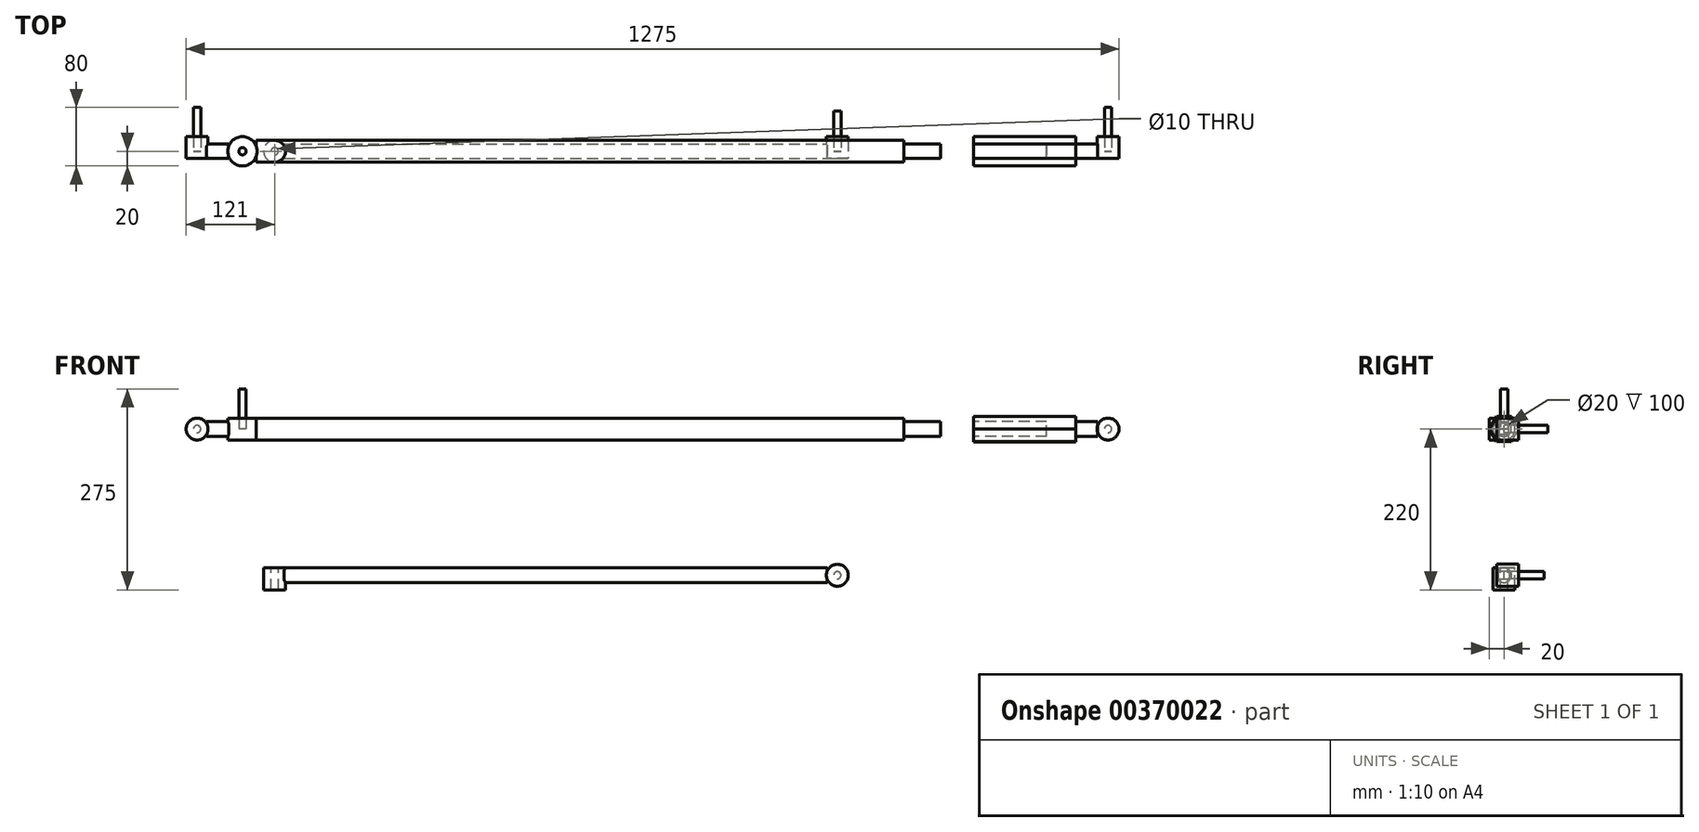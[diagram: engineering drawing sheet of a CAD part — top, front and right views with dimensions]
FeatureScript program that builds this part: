
annotation { "Feature Type Name" : "Feature", "Feature Type Description" : "" }
export const myFeature = defineFeature(function(context is Context, id is Id, definition is map)
    precondition{}
    {
        {
            var Q0;
            Q0=qCreatedBy(makeId("Right.planeOp"),FACE);
            var sketch = newSketch(context, id + "F0", { "sketchPlane" : qUnion([Q0])});
            skCircle(sketch, "E0", {"center": v(0, 0) * mm, "radius": 20 * mm});
            skCircle(sketch, "E1.cCircle", {"center": v(0, 0) * mm, "radius": 20 * mm, "construction": true});
            skLineSegment(sketch, "E1.0", {"start": v(10.09, 17.27) * mm, "end": v(20, -0.1) * mm});
            skLineSegment(sketch, "E1.1", {"start": v(20, -0.1) * mm, "end": v(9.91, -17.37) * mm});
            skLineSegment(sketch, "E1.2", {"start": v(9.91, -17.37) * mm, "end": v(-10.09, -17.27) * mm});
            skLineSegment(sketch, "E1.3", {"start": v(-10.09, -17.27) * mm, "end": v(-20, 0.1) * mm});
            skLineSegment(sketch, "E1.4", {"start": v(-20, 0.1) * mm, "end": v(-9.91, 17.37) * mm});
            skLineSegment(sketch, "E1.5", {"start": v(-9.91, 17.37) * mm, "end": v(10.09, 17.27) * mm});
            skCircle(sketch, "E2", {"center": v(0, 0) * mm, "radius": 10 * mm});
            skSolve(sketch);
        }
        {
            var Q0;
            Q0=makeQuery(id+"F0.imprint","IMPRINT",FACE,{"disambiguationData":[TD([[makeQuery(id+"F0.imprint","IMPRINT",EDGE,{"derivedFrom":sQuery(id+"F0.wireOp",EDGE,"E1.0")}),-1.0]])]});
            extrude(context, id + "F1", {"entities" : qUnion([Q0]), "depth" : 140 * mm});
        }
        {
            var Q0;
            Q0=qCreatedBy(makeId("Right.planeOp"),FACE);
            cPlane(context, id + "F2", {"entities" : qUnion([Q0]), "cplaneType" : CPlaneType.OFFSET, "offset" : 100 * mm, "width" : 150 * mm, "height" : 150 * mm});
        }
        {
            var Q0;
            Q0=qCreatedBy(id+"F2.planeOp",FACE);
            var sketch = newSketch(context, id + "F3", { "sketchPlane" : qUnion([Q0])});
            skCircle(sketch, "E3.0", {"center": v(0, 0) * mm, "radius": 10 * mm});
            skSolve(sketch);
        }
        {
            var Q0;
            Q0=qSketchRegion(id+"F3",true);
            extrude(context, id + "F4", {"entities" : qUnion([Q0]), "operationType" : NewBodyOperationType.ADD, "depth" : 70 * mm});
        }
        {
            var Q0;
            Q0=qCreatedBy(makeId("Front.planeOp"),FACE);
            cPlane(context, id + "F5", {"entities" : qUnion([Q0]), "cplaneType" : CPlaneType.OFFSET, "offset" : 10 * mm, "width" : 150 * mm, "height" : 150 * mm});
        }
        {
            var Q0;
            Q0=qCreatedBy(id+"F5.planeOp",FACE);
            var sketch = newSketch(context, id + "F6", { "sketchPlane" : qUnion([Q0])});
            skLineSegment(sketch, "E4", {"start": v(0, 0) * mm, "end": v(184, 0) * mm});
            skCircle(sketch, "E5", {"center": v(184, 0) * mm, "radius": 15 * mm});
            skSolve(sketch);
        }
        {
            var Q0;
            Q0=qSketchRegion(id+"F6",true);
            extrude(context, id + "F7", {"entities" : qUnion([Q0]), "oppositeDirection" : true, "depth" : 30 * mm});
        }
        {
            var Q0;
            Q0=qCreatedBy(makeId("Front.planeOp"),FACE);
            var sketch = newSketch(context, id + "F8", { "sketchPlane" : qUnion([Q0])});
            skLineSegment(sketch, "E6", {"start": v(0, 0) * mm, "end": v(184, 0) * mm});
            skCircle(sketch, "E7", {"center": v(184, 0) * mm, "radius": 5 * mm});
            skSolve(sketch);
        }
        {
            var Q0;
            Q0=qSketchRegion(id+"F8",true);
            extrude(context, id + "F9", {"entities" : qUnion([Q0]), "oppositeDirection" : true, "depth" : 60 * mm});
        }
        {
            var Q0;
            Q0=qCreatedBy(makeId("Front.planeOp"),FACE);
            var sketch = newSketch(context, id + "F10", { "sketchPlane" : qUnion([Q0])});
            skLineSegment(sketch, "E8", {"start": v(-45, 0) * mm, "end": v(-980, 0) * mm});
            skLineSegment(sketch, "E9", {"start": v(-45, 0) * mm, "end": v(-45, 10) * mm});
            skLineSegment(sketch, "E10", {"start": v(-45, 10) * mm, "end": v(-95, 10) * mm});
            skLineSegment(sketch, "E11", {"start": v(-95, 10) * mm, "end": v(-95, 15) * mm});
            skLineSegment(sketch, "E12", {"start": v(-95, 15) * mm, "end": v(-980, 15) * mm});
            skLineSegment(sketch, "E13", {"start": v(-980, 15) * mm, "end": v(-980, 0) * mm});
            skSolve(sketch);
        }
        {
            var Q0;
            Q0=makeQuery(id+"F10.imprint","IMPRINT",FACE,{"disambiguationData":[TD([[makeQuery(id+"F10.imprint","IMPRINT",EDGE,{"derivedFrom":sQuery(id+"F10.wireOp",EDGE,"E8")}),-1.0]])]});
            var Q1;
            Q1=sQuery(id+"F10.wireOp",EDGE,"E8");
            revolve(context, id + "F11", {"entities" : qUnion([Q0]), "axis" : qUnion([Q1]), "revolveType" : RevolveType.FULL});
        }
        {
            var Q0;
            Q0=qCreatedBy(makeId("Top.planeOp"),FACE);
            cPlane(context, id + "F12", {"entities" : qUnion([Q0]), "cplaneType" : CPlaneType.OFFSET, "offset" : 15 * mm, "width" : 150 * mm, "height" : 150 * mm});
        }
        {
            var Q0;
            Q0=qCreatedBy(id+"F12.planeOp",FACE);
            var sketch = newSketch(context, id + "F13", { "sketchPlane" : qUnion([Q0])});
            skLineSegment(sketch, "E14", {"start": v(0, 0) * mm, "end": v(-999, 0) * mm});
            skCircle(sketch, "E15", {"center": v(-999, 0) * mm, "radius": 20 * mm});
            skSolve(sketch);
        }
        {
            var Q0;
            Q0=qSketchRegion(id+"F13",true);
            extrude(context, id + "F14", {"entities" : qUnion([Q0]), "operationType" : NewBodyOperationType.ADD, "oppositeDirection" : true, "depth" : 30 * mm});
        }
        {
            var Q0;
            Q0=qCreatedBy(makeId("Top.planeOp"),FACE);
            var sketch = newSketch(context, id + "F15", { "sketchPlane" : qUnion([Q0])});
            skLineSegment(sketch, "E16", {"start": v(0, 0) * mm, "end": v(-999, 0) * mm});
            skCircle(sketch, "E17", {"center": v(-999, 0) * mm, "radius": 5 * mm});
            skSolve(sketch);
        }
        {
            var Q0;
            Q0=qSketchRegion(id+"F15",true);
            extrude(context, id + "F16", {"entities" : qUnion([Q0]), "depth" : 55 * mm});
        }
        {
            var Q0;
            Q0=qCreatedBy(makeId("Top.planeOp"),FACE);
            var sketch = newSketch(context, id + "F17", { "sketchPlane" : qUnion([Q0])});
            skLineSegment(sketch, "E18", {"start": v(0, 0) * mm, "end": v(-1018, 0) * mm});
            skLineSegment(sketch, "E19", {"start": v(-1018, 0) * mm, "end": v(-1048, 0) * mm});
            skLineSegment(sketch, "E20", {"start": v(-1048, 0) * mm, "end": v(-1048, 10) * mm});
            skLineSegment(sketch, "E21", {"start": v(-1048, 10) * mm, "end": v(-1018, 10) * mm});
            skLineSegment(sketch, "E22", {"start": v(-1018, 10) * mm, "end": v(-1018, 0) * mm});
            skSolve(sketch);
        }
        {
            var Q0;
            Q0=qSketchRegion(id+"F17",true);
            var Q1;
            Q1=sQuery(id+"F17.wireOp",EDGE,"E19");
            revolve(context, id + "F18", {"operationType" : NewBodyOperationType.ADD, "entities" : qUnion([Q0]), "axis" : qUnion([Q1]), "revolveType" : RevolveType.FULL});
        }
        {
            var Q0;
            Q0=qCreatedBy(id+"F5.planeOp",FACE);
            var sketch = newSketch(context, id + "F19", { "sketchPlane" : qUnion([Q0])});
            skLineSegment(sketch, "E23", {"start": v(0, 0) * mm, "end": v(-1061, 0) * mm});
            skCircle(sketch, "E24", {"center": v(-1061, 0) * mm, "radius": 15 * mm});
            skSolve(sketch);
        }
        {
            var Q0;
            Q0=qSketchRegion(id+"F19",true);
            extrude(context, id + "F20", {"entities" : qUnion([Q0]), "operationType" : NewBodyOperationType.ADD, "oppositeDirection" : true, "depth" : 30 * mm});
        }
        {
            var Q0;
            Q0=qCreatedBy(makeId("Front.planeOp"),FACE);
            var sketch = newSketch(context, id + "F21", { "sketchPlane" : qUnion([Q0])});
            skLineSegment(sketch, "E25", {"start": v(0, 0) * mm, "end": v(-1061, 0) * mm});
            skCircle(sketch, "E26", {"center": v(-1061, 0) * mm, "radius": 5 * mm});
            skSolve(sketch);
        }
        {
            var Q0;
            Q0=qSketchRegion(id+"F21",true);
            extrude(context, id + "F22", {"entities" : qUnion([Q0]), "oppositeDirection" : true, "depth" : 60 * mm});
        }
        {
            var Q0;
            Q0=qCreatedBy(makeId("Front.planeOp"),FACE);
            var sketch = newSketch(context, id + "F23", { "sketchPlane" : qUnion([Q0])});
            skLineSegment(sketch, "E27", {"start": v(0, 0) * mm, "end": v(0, -200) * mm});
            skLineSegment(sketch, "E28", {"start": v(0, -200) * mm, "end": v(-200, -200) * mm});
            skLineSegment(sketch, "E29", {"start": v(-200, -200) * mm, "end": v(-942, -200) * mm});
            skLineSegment(sketch, "E30", {"start": v(-942, -200) * mm, "end": v(-942, -190) * mm});
            skLineSegment(sketch, "E31", {"start": v(-942, -190) * mm, "end": v(-200, -190) * mm});
            skLineSegment(sketch, "E32", {"start": v(-200, -190) * mm, "end": v(-200, -200) * mm});
            skSolve(sketch);
        }
        {
            var Q0;
            Q0=qSketchRegion(id+"F23",true);
            var Q1;
            Q1=sQuery(id+"F23.wireOp",EDGE,"E29");
            revolve(context, id + "F24", {"entities" : qUnion([Q0]), "axis" : qUnion([Q1]), "revolveType" : RevolveType.FULL});
        }
        {
            var Q0;
            Q0=qCreatedBy(id+"F5.planeOp",FACE);
            var sketch = newSketch(context, id + "F25", { "sketchPlane" : qUnion([Q0])});
            skLineSegment(sketch, "E33", {"start": v(0, 0) * mm, "end": v(0, -200) * mm});
            skLineSegment(sketch, "E34", {"start": v(0, -200) * mm, "end": v(-186, -200) * mm});
            skCircle(sketch, "E35", {"center": v(-186, -200) * mm, "radius": 15 * mm});
            skSolve(sketch);
        }
        {
            var Q0;
            Q0=qSketchRegion(id+"F25",true);
            extrude(context, id + "F26", {"entities" : qUnion([Q0]), "operationType" : NewBodyOperationType.ADD, "oppositeDirection" : true, "depth" : 30 * mm});
        }
        {
            var Q0;
            Q0=qCreatedBy(makeId("Front.planeOp"),FACE);
            var sketch = newSketch(context, id + "F27", { "sketchPlane" : qUnion([Q0])});
            skLineSegment(sketch, "E36", {"start": v(0, 0) * mm, "end": v(0, -200) * mm});
            skLineSegment(sketch, "E37", {"start": v(0, -200) * mm, "end": v(-186, -200) * mm});
            skCircle(sketch, "E38", {"center": v(-186, -200) * mm, "radius": 5 * mm});
            skSolve(sketch);
        }
        {
            var Q0;
            Q0=qSketchRegion(id+"F27",true);
            extrude(context, id + "F28", {"entities" : qUnion([Q0]), "oppositeDirection" : true, "depth" : 55 * mm});
        }
        {
            var Q0;
            Q0=qCreatedBy(makeId("Top.planeOp"),FACE);
            cPlane(context, id + "F29", {"entities" : qUnion([Q0]), "cplaneType" : CPlaneType.OFFSET, "offset" : 190 * mm, "oppositeDirection" : true, "width" : 150 * mm, "height" : 150 * mm});
        }
        {
            var Q0;
            Q0=qCreatedBy(id+"F29.planeOp",FACE);
            var sketch = newSketch(context, id + "F30", { "sketchPlane" : qUnion([Q0])});
            skLineSegment(sketch, "E39", {"start": v(0, 0) * mm, "end": v(-955, 0) * mm});
            skCircle(sketch, "E40", {"center": v(-955, 0) * mm, "radius": 15 * mm});
            skCircle(sketch, "E41", {"center": v(-955, 0) * mm, "radius": 5 * mm});
            skSolve(sketch);
        }
        {
            var Q0;
            Q0=qSketchRegion(id+"F30",true);
            extrude(context, id + "F31", {"entities" : qUnion([Q0]), "operationType" : NewBodyOperationType.ADD, "oppositeDirection" : true, "depth" : 30 * mm});
        }
    });
